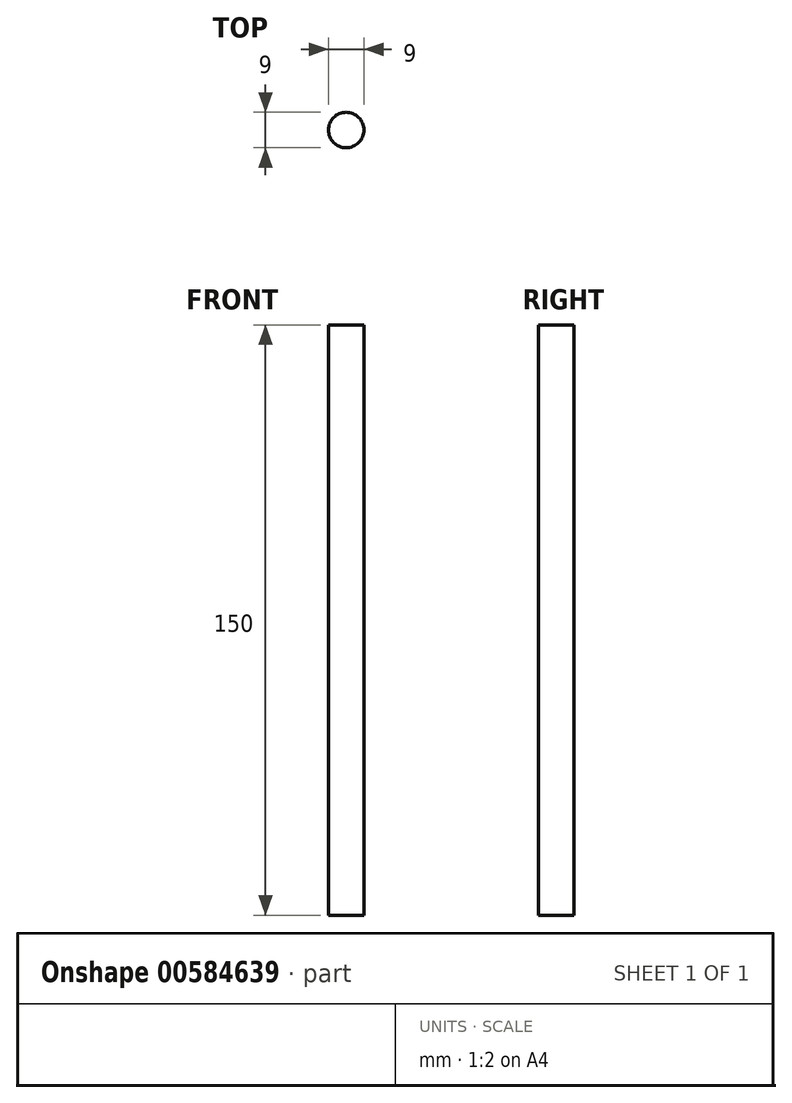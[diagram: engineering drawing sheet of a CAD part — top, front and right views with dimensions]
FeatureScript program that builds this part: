
annotation { "Feature Type Name" : "Feature", "Feature Type Description" : "" }
export const myFeature = defineFeature(function(context is Context, id is Id, definition is map)
    precondition{}
    {
        {
            var Q0;
            Q0=qCreatedBy(makeId("Top.planeOp"),FACE);
            var sketch = newSketch(context, id + "F0", { "sketchPlane" : qUnion([Q0])});
            skCircle(sketch, "E0", {"center": v(0, 0) * mm, "radius": 4.5 * mm});
            skSolve(sketch);
        }
        {
            var Q0;
            Q0=makeQuery(id+"F0.imprint","IMPRINT",FACE,{"disambiguationData":[TD([[makeQuery(id+"F0.imprint","IMPRINT",EDGE,{"derivedFrom":sQuery(id+"F0.wireOp",EDGE,"E0")}),1.0]])]});
            extrude(context, id + "F1", {"entities" : qUnion([Q0]), "depth" : 150 * mm, "offsetDistance" : 25 * mm});
        }
    });
